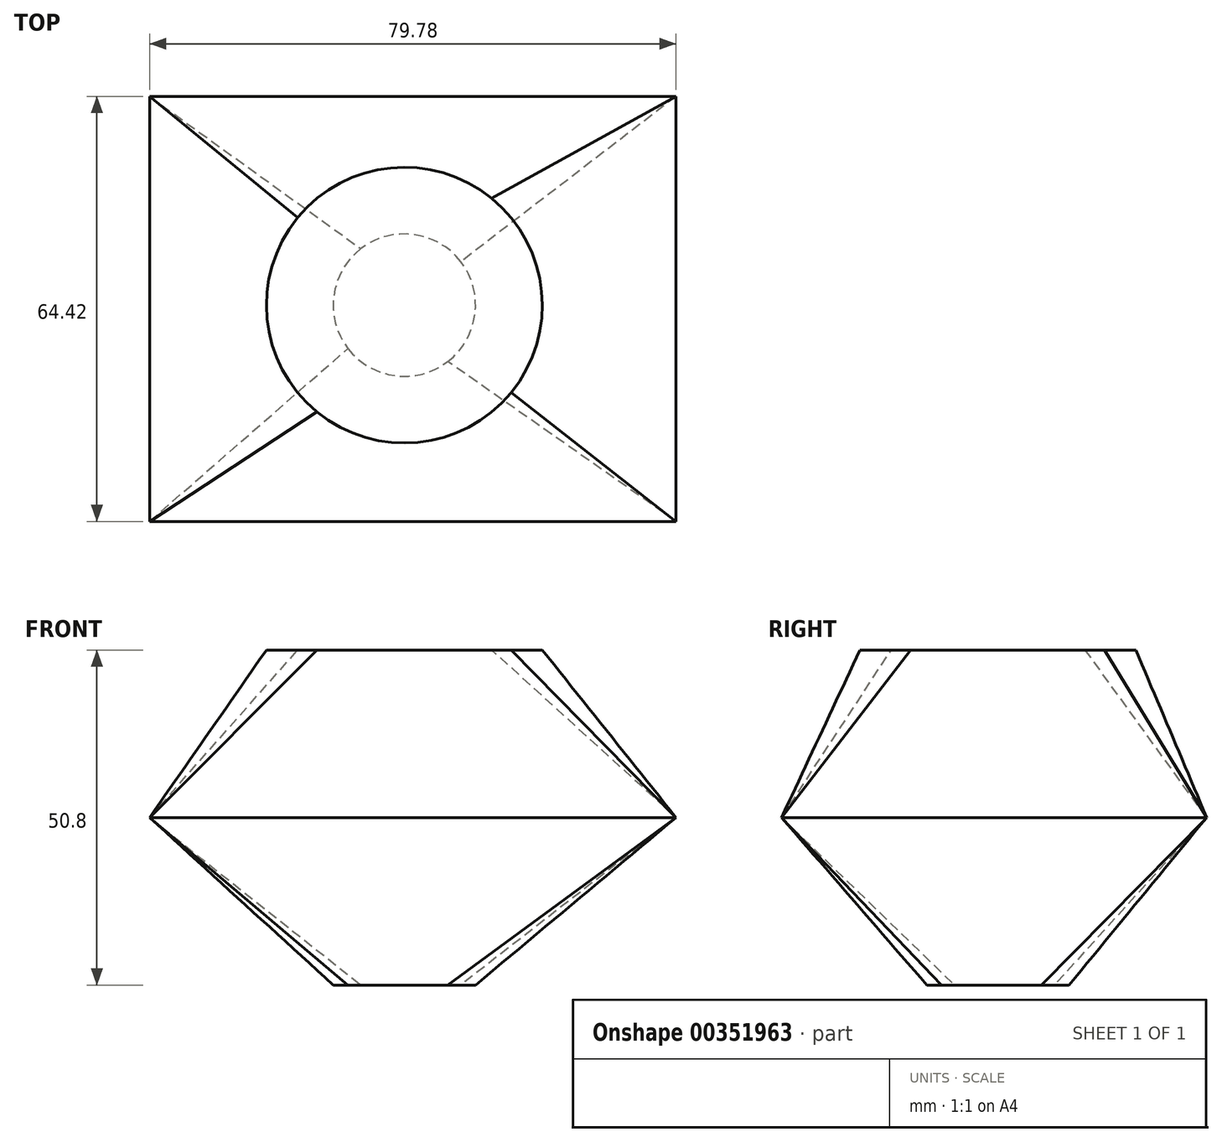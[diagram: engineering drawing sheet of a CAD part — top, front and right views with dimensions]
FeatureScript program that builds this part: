
annotation { "Feature Type Name" : "Feature", "Feature Type Description" : "" }
export const myFeature = defineFeature(function(context is Context, id is Id, definition is map)
    precondition{}
    {
        {
            var Q0;
            Q0=qCreatedBy(makeId("Top.planeOp"),FACE);
            cPlane(context, id + "F0", {"entities" : qUnion([Q0]), "cplaneType" : CPlaneType.OFFSET, "offset" : 50.8 * mm, "width" : 152.4 * mm, "height" : 152.4 * mm});
        }
        {
            var Q0;
            Q0=qCreatedBy(makeId("Top.planeOp"),FACE);
            cPlane(context, id + "F1", {"entities" : qUnion([Q0]), "cplaneType" : CPlaneType.OFFSET, "offset" : 25.4 * mm, "width" : 152.4 * mm, "height" : 152.4 * mm});
        }
        {
            var Q0;
            Q0=qCreatedBy(id+"F0.planeOp",FACE);
            var sketch = newSketch(context, id + "F2", { "sketchPlane" : qUnion([Q0])});
            skCircle(sketch, "E0", {"center": v(0, 0) * mm, "radius": 20.9 * mm});
            skSolve(sketch);
        }
        {
            var Q0;
            Q0=qCreatedBy(id+"F1.planeOp",FACE);
            var sketch = newSketch(context, id + "F3", { "sketchPlane" : qUnion([Q0])});
            skLineSegment(sketch, "E1.bottom", {"start": v(-38.6, 31.63) * mm, "end": v(41.17, 31.63) * mm});
            skLineSegment(sketch, "E1.top", {"start": v(-38.6, -32.8) * mm, "end": v(41.17, -32.8) * mm});
            skLineSegment(sketch, "E1.left", {"start": v(-38.6, 31.63) * mm, "end": v(-38.6, -32.8) * mm});
            skLineSegment(sketch, "E1.right", {"start": v(41.17, 31.63) * mm, "end": v(41.17, -32.8) * mm});
            skSolve(sketch);
        }
        {
            var Q0;
            Q0=qCreatedBy(makeId("Top.planeOp"),FACE);
            var sketch = newSketch(context, id + "F4", { "sketchPlane" : qUnion([Q0])});
            skCircle(sketch, "E2", {"center": v(0, 0) * mm, "radius": 10.79 * mm});
            skSolve(sketch);
        }
        {
            var Q0;
            Q0=makeQuery(id+"F3.imprint","IMPRINT",FACE,{"disambiguationData":[TD([[makeQuery(id+"F3.imprint","IMPRINT",EDGE,{"derivedFrom":sQuery(id+"F3.wireOp",EDGE,"E1.bottom")}),-1.0]])]});
            var Q1;
            Q1=makeQuery(id+"F2.imprint","IMPRINT",FACE,{"disambiguationData":[TD([[makeQuery(id+"F2.imprint","IMPRINT",EDGE,{"derivedFrom":sQuery(id+"F2.wireOp",EDGE,"E0")}),1.0]])]});
            loft(context, id + "F5", {"sheetProfilesArray" : [{ "sheetProfileEntities" : qUnion([Q0]) }, { "sheetProfileEntities" : qUnion([Q1]) }]});
        }
        {
            var Q1;
            Q1=makeQuery(id+"F5.opLoft","CAP_FACE",FACE,{"disambiguationData":[OSD([makeQuery(id+"F3.imprint","IMPRINT",FACE,{"disambiguationData":[TD([[makeQuery(id+"F3.imprint","IMPRINT",EDGE,{"derivedFrom":sQuery(id+"F3.wireOp",EDGE,"E1.bottom")}),-1.0]])]})])],"isStart":true});
            var Q2;
            Q2=makeQuery(id+"F4.imprint","IMPRINT",FACE,{"disambiguationData":[TD([[makeQuery(id+"F4.imprint","IMPRINT",EDGE,{"derivedFrom":sQuery(id+"F4.wireOp",EDGE,"E2")}),1.0]])]});
            loft(context, id + "F6", {"operationType" : NewBodyOperationType.ADD, "sheetProfilesArray" : [{ "sheetProfileEntities" : qUnion([Q1]) }, { "sheetProfileEntities" : qUnion([Q2]) }]});
        }
    });
